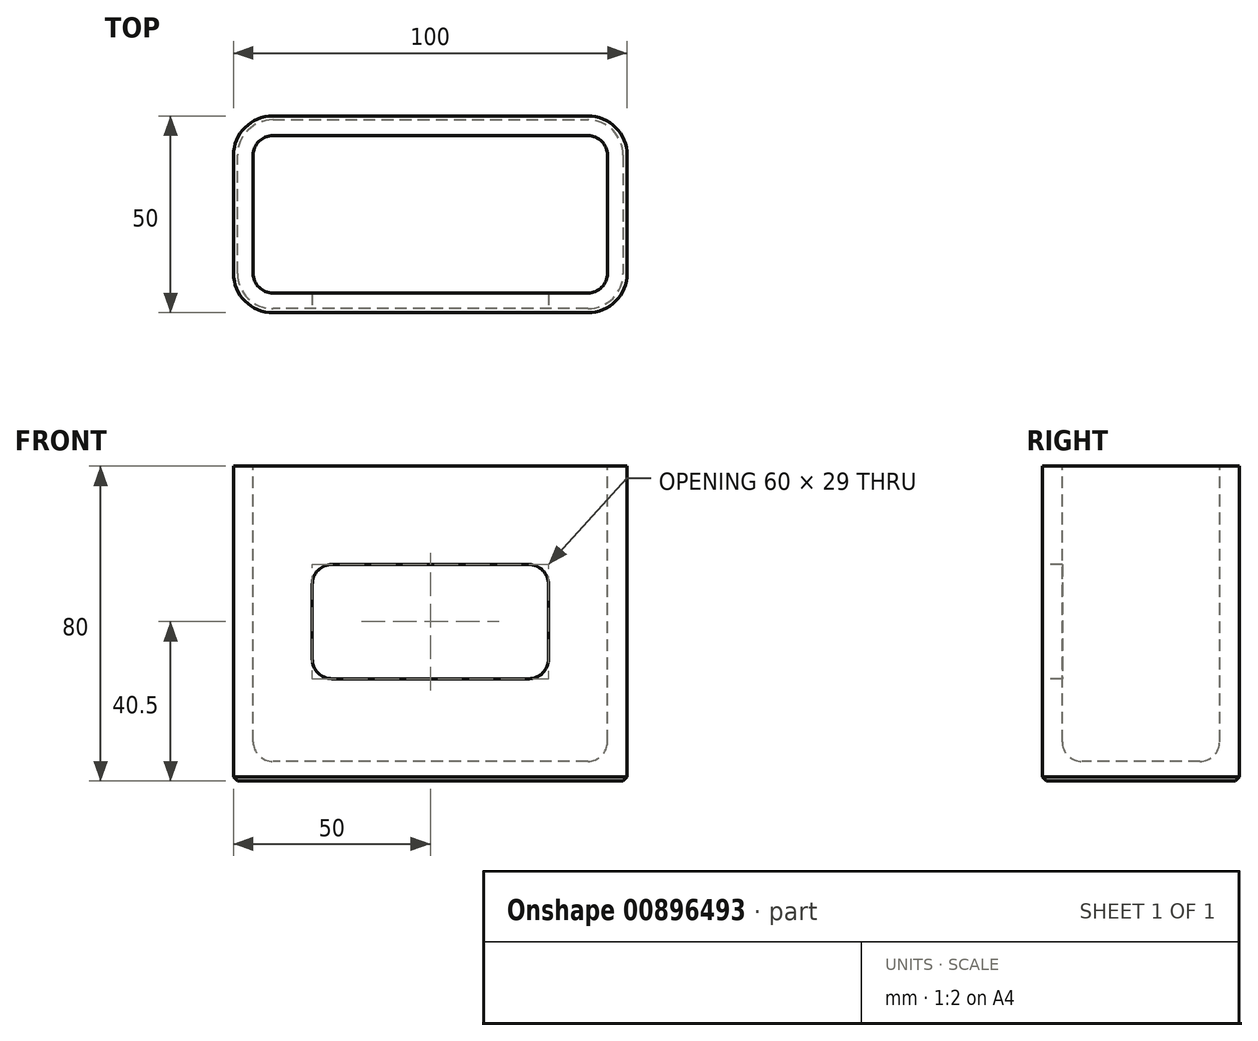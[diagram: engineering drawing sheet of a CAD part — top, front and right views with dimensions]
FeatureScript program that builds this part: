
annotation { "Feature Type Name" : "Feature", "Feature Type Description" : "" }
export const myFeature = defineFeature(function(context is Context, id is Id, definition is map)
    precondition{}
    {
        {
            var Q0;
            Q0=qCreatedBy(makeId("Top.planeOp"),FACE);
            var sketch = newSketch(context, id + "F0", { "sketchPlane" : qUnion([Q0])});
            skLineSegment(sketch, "E0.bottom", {"start": v(50, 25) * mm, "end": v(-50, 25) * mm});
            skLineSegment(sketch, "E0.top", {"start": v(50, -25) * mm, "end": v(-50, -25) * mm});
            skLineSegment(sketch, "E0.left", {"start": v(50, 25) * mm, "end": v(50, -25) * mm});
            skLineSegment(sketch, "E0.right", {"start": v(-50, 25) * mm, "end": v(-50, -25) * mm});
            skPoint(sketch, "E0.middle", {"position": v(0, 0) * mm});
            skSolve(sketch);
        }
        {
            var Q0;
            Q0 = qSketchRegion(id + "F0", true);
            extrude(context, id + "F1", {"entities" : qUnion([Q0]), "depth" : 80 * mm, "offsetDistance" : 25 * mm});
        }
        {
            var Q0;
            Q0=makeQuery(id+"F1.opExtrude","CAP_FACE",FACE,{"disambiguationData":[OSD([sQuery(id+"F0.wireOp",EDGE,"E0.bottom"),sQuery(id+"F0.wireOp",EDGE,"E0.top"),sQuery(id+"F0.wireOp",EDGE,"E0.left"),sQuery(id+"F0.wireOp",EDGE,"E0.right")])],"isStart":false});
            var sketch = newSketch(context, id + "F2", { "sketchPlane" : qUnion([Q0])});
            skLineSegment(sketch, "E1", {"start": v(-45, 20) * mm, "end": v(-45, -20) * mm});
            skLineSegment(sketch, "E2", {"start": v(-45, -20) * mm, "end": v(45, -20) * mm});
            skLineSegment(sketch, "E3", {"start": v(45, -20) * mm, "end": v(45, 20) * mm});
            skLineSegment(sketch, "E4", {"start": v(45, 20) * mm, "end": v(-45, 20) * mm});
            skSolve(sketch);
        }
        {
            var Q0;
            Q0 = qSketchRegion(id + "F2", true);
            extrude(context, id + "F3", {"entities" : qUnion([Q0]), "operationType" : NewBodyOperationType.REMOVE, "oppositeDirection" : true, "depth" : 75 * mm, "offsetDistance" : 25 * mm});
        }
        {
            var Q0;
            Q0=makeQuery(id+"F3.boolean.opBoolean","COPY",EDGE,{"derivedFrom":makeQuery(id+"F3.opExtrude","CAP_EDGE",EDGE,{"disambiguationData":[OSD([sQuery(id+"F2.wireOp",EDGE,"E3")])],"isStart":false})});
            var Q1;
            Q1=makeQuery(id+"F3.boolean.opBoolean","COPY",EDGE,{"derivedFrom":makeQuery(id+"F3.opExtrude","CAP_EDGE",EDGE,{"disambiguationData":[OSD([sQuery(id+"F2.wireOp",EDGE,"E4")])],"isStart":false})});
            var Q2;
            Q2=makeQuery(id+"F3.boolean.opBoolean","COPY",EDGE,{"derivedFrom":makeQuery(id+"F3.opExtrude","CAP_EDGE",EDGE,{"disambiguationData":[OSD([sQuery(id+"F2.wireOp",EDGE,"E2")])],"isStart":false})});
            var Q3;
            Q3=makeQuery(id+"F3.boolean.opBoolean","COPY",EDGE,{"derivedFrom":makeQuery(id+"F3.opExtrude","CAP_EDGE",EDGE,{"disambiguationData":[OSD([sQuery(id+"F2.wireOp",EDGE,"E1")])],"isStart":false})});
            var Q4;
            Q4=makeQuery(id+"F3.boolean.opBoolean","COPY",EDGE,{"derivedFrom":makeQuery(id+"F3.opExtrude","SWEPT_EDGE",EDGE,{"disambiguationData":[OSD([sQuery(id+"F2.wireOp",EDGE,"E1"),sQuery(id+"F2.wireOp",EDGE,"E4")])]})});
            var Q5;
            Q5=makeQuery(id+"F3.boolean.opBoolean","COPY",EDGE,{"derivedFrom":makeQuery(id+"F3.opExtrude","SWEPT_EDGE",EDGE,{"disambiguationData":[OSD([sQuery(id+"F2.wireOp",EDGE,"E1"),sQuery(id+"F2.wireOp",EDGE,"E2")])]})});
            var Q6;
            Q6=makeQuery(id+"F3.boolean.opBoolean","COPY",EDGE,{"derivedFrom":makeQuery(id+"F3.opExtrude","SWEPT_EDGE",EDGE,{"disambiguationData":[OSD([sQuery(id+"F2.wireOp",EDGE,"E3"),sQuery(id+"F2.wireOp",EDGE,"E4")])]})});
            var Q7;
            Q7=makeQuery(id+"F3.boolean.opBoolean","COPY",EDGE,{"derivedFrom":makeQuery(id+"F3.opExtrude","SWEPT_EDGE",EDGE,{"disambiguationData":[OSD([sQuery(id+"F2.wireOp",EDGE,"E2"),sQuery(id+"F2.wireOp",EDGE,"E3")])]})});
            var Q8;
            Q8=makeQuery(id+"F3.boolean.opBoolean","COPY",EDGE,{"derivedFrom":makeQuery(id+"F3.opExtrude","CAP_EDGE",EDGE,{"disambiguationData":[OSD([sQuery(id+"F2.wireOp",EDGE,"E3")])],"isStart":true})});
            var Q9;
            Q9=makeQuery(id+"F3.boolean.opBoolean","COPY",EDGE,{"derivedFrom":makeQuery(id+"F3.opExtrude","CAP_EDGE",EDGE,{"disambiguationData":[OSD([sQuery(id+"F2.wireOp",EDGE,"E4")])],"isStart":true})});
            var Q10;
            Q10=makeQuery(id+"F3.boolean.opBoolean","COPY",EDGE,{"derivedFrom":makeQuery(id+"F3.opExtrude","CAP_EDGE",EDGE,{"disambiguationData":[OSD([sQuery(id+"F2.wireOp",EDGE,"E1")])],"isStart":true})});
            var Q11;
            Q11=makeQuery(id+"F3.boolean.opBoolean","COPY",EDGE,{"derivedFrom":makeQuery(id+"F3.opExtrude","CAP_EDGE",EDGE,{"disambiguationData":[OSD([sQuery(id+"F2.wireOp",EDGE,"E2")])],"isStart":true})});
            fillet(context, id + "F4", {"entities" : qUnion([Q0, Q1, Q2, Q3, Q4, Q5, Q6, Q7, Q8, Q9, Q10, Q11]), "radius" : 5 * mm, "tangentPropagation" : true, "allowEdgeOverflow" : false});
        }
        {
            var Q0;
            Q0=makeQuery(id+"F1.opExtrude","SWEPT_EDGE",EDGE,{"disambiguationData":[OSD([sQuery(id+"F0.wireOp",EDGE,"E0.top"),sQuery(id+"F0.wireOp",EDGE,"E0.left")])]});
            var Q1;
            Q1=makeQuery(id+"F1.opExtrude","SWEPT_EDGE",EDGE,{"disambiguationData":[OSD([sQuery(id+"F0.wireOp",EDGE,"E0.top"),sQuery(id+"F0.wireOp",EDGE,"E0.right")])]});
            var Q2;
            Q2=makeQuery(id+"F1.opExtrude","SWEPT_EDGE",EDGE,{"disambiguationData":[OSD([sQuery(id+"F0.wireOp",EDGE,"E0.bottom"),sQuery(id+"F0.wireOp",EDGE,"E0.right")])]});
            var Q3;
            Q3=makeQuery(id+"F1.opExtrude","SWEPT_EDGE",EDGE,{"disambiguationData":[OSD([sQuery(id+"F0.wireOp",EDGE,"E0.bottom"),sQuery(id+"F0.wireOp",EDGE,"E0.left")])]});
            fillet(context, id + "F5", {"entities" : qUnion([Q0, Q1, Q2, Q3]), "radius" : 10 * mm, "tangentPropagation" : true, "allowEdgeOverflow" : false});
        }
        {
            var Q0;
            Q0=makeQuery(id+"F1.opExtrude","CAP_EDGE",EDGE,{"disambiguationData":[OSD([sQuery(id+"F0.wireOp",EDGE,"E0.top")])],"isStart":true});
            var Q1;
            {var subQ0=sQuery(id+"F0.wireOp",EDGE,"E0.left");var subQ1=sQuery(id+"F0.wireOp",EDGE,"E0.top");Q1=makeQuery(id+"F5.opFillet","BLEND_EDGE",EDGE,{"blendedFrom":[makeQuery(id+"F1.opExtrude","SWEPT_EDGE",EDGE,{"disambiguationData":[OSD([subQ1,subQ0])]}),makeQuery(id+"F1.opExtrude","CAP_FACE",FACE,{"disambiguationData":[OSD([sQuery(id+"F0.wireOp",EDGE,"E0.bottom"),subQ1,subQ0,sQuery(id+"F0.wireOp",EDGE,"E0.right")])],"isStart":true})],"blendedInto":[makeQuery(id+"F1.opExtrude","CAP_FACE",FACE,{"disambiguationData":[OSD([sQuery(id+"F0.wireOp",EDGE,"E0.bottom"),subQ1,subQ0,sQuery(id+"F0.wireOp",EDGE,"E0.right")])],"isStart":true})]});}
            var Q2;
            Q2=makeQuery(id+"F1.opExtrude","CAP_EDGE",EDGE,{"disambiguationData":[OSD([sQuery(id+"F0.wireOp",EDGE,"E0.left")])],"isStart":true});
            var Q3;
            {var subQ0=sQuery(id+"F0.wireOp",EDGE,"E0.left");var subQ1=sQuery(id+"F0.wireOp",EDGE,"E0.bottom");Q3=makeQuery(id+"F5.opFillet","BLEND_EDGE",EDGE,{"blendedFrom":[makeQuery(id+"F1.opExtrude","SWEPT_EDGE",EDGE,{"disambiguationData":[OSD([subQ1,subQ0])]}),makeQuery(id+"F1.opExtrude","CAP_FACE",FACE,{"disambiguationData":[OSD([subQ1,sQuery(id+"F0.wireOp",EDGE,"E0.top"),subQ0,sQuery(id+"F0.wireOp",EDGE,"E0.right")])],"isStart":true})],"blendedInto":[makeQuery(id+"F1.opExtrude","CAP_FACE",FACE,{"disambiguationData":[OSD([subQ1,sQuery(id+"F0.wireOp",EDGE,"E0.top"),subQ0,sQuery(id+"F0.wireOp",EDGE,"E0.right")])],"isStart":true})]});}
            var Q4;
            Q4=makeQuery(id+"F1.opExtrude","CAP_EDGE",EDGE,{"disambiguationData":[OSD([sQuery(id+"F0.wireOp",EDGE,"E0.bottom")])],"isStart":true});
            var Q5;
            {var subQ0=sQuery(id+"F0.wireOp",EDGE,"E0.right");var subQ1=sQuery(id+"F0.wireOp",EDGE,"E0.bottom");Q5=makeQuery(id+"F5.opFillet","BLEND_EDGE",EDGE,{"blendedFrom":[makeQuery(id+"F1.opExtrude","SWEPT_EDGE",EDGE,{"disambiguationData":[OSD([subQ1,subQ0])]}),makeQuery(id+"F1.opExtrude","CAP_FACE",FACE,{"disambiguationData":[OSD([subQ1,sQuery(id+"F0.wireOp",EDGE,"E0.top"),sQuery(id+"F0.wireOp",EDGE,"E0.left"),subQ0])],"isStart":true})],"blendedInto":[makeQuery(id+"F1.opExtrude","CAP_FACE",FACE,{"disambiguationData":[OSD([subQ1,sQuery(id+"F0.wireOp",EDGE,"E0.top"),sQuery(id+"F0.wireOp",EDGE,"E0.left"),subQ0])],"isStart":true})]});}
            var Q6;
            Q6=makeQuery(id+"F1.opExtrude","CAP_EDGE",EDGE,{"disambiguationData":[OSD([sQuery(id+"F0.wireOp",EDGE,"E0.right")])],"isStart":true});
            var Q7;
            {var subQ0=sQuery(id+"F0.wireOp",EDGE,"E0.right");var subQ1=sQuery(id+"F0.wireOp",EDGE,"E0.top");Q7=makeQuery(id+"F5.opFillet","BLEND_EDGE",EDGE,{"blendedFrom":[makeQuery(id+"F1.opExtrude","SWEPT_EDGE",EDGE,{"disambiguationData":[OSD([subQ1,subQ0])]}),makeQuery(id+"F1.opExtrude","CAP_FACE",FACE,{"disambiguationData":[OSD([sQuery(id+"F0.wireOp",EDGE,"E0.bottom"),subQ1,sQuery(id+"F0.wireOp",EDGE,"E0.left"),subQ0])],"isStart":true})],"blendedInto":[makeQuery(id+"F1.opExtrude","CAP_FACE",FACE,{"disambiguationData":[OSD([sQuery(id+"F0.wireOp",EDGE,"E0.bottom"),subQ1,sQuery(id+"F0.wireOp",EDGE,"E0.left"),subQ0])],"isStart":true})]});}
            chamfer(context, id + "F6", {"entities" : qUnion([Q0, Q1, Q2, Q3, Q4, Q5, Q6, Q7]), "width" : 1 * mm, "tangentPropagation" : true});
        }
        {
            var Q0;
            Q0=makeQuery(id+"F1.opExtrude","SWEPT_FACE",FACE,{"disambiguationData":[OSD([sQuery(id+"F0.wireOp",EDGE,"E0.top")])]});
            var sketch = newSketch(context, id + "F7", { "sketchPlane" : qUnion([Q0])});
            skLineSegment(sketch, "E5.bottom", {"start": v(-25, 55) * mm, "end": v(25, 55) * mm});
            skLineSegment(sketch, "E5.top", {"start": v(-25, 26) * mm, "end": v(25, 26) * mm});
            skLineSegment(sketch, "E5.left", {"start": v(-30, 50) * mm, "end": v(-30, 31) * mm});
            skLineSegment(sketch, "E5.right", {"start": v(30, 50) * mm, "end": v(30, 31) * mm});
            skPoint(sketch, "E6.visualSharp", {"position": v(-30, 55) * mm});
            skArc(sketch, "E6.filletArc", {"start": v(-25, 55) * mm, "mid": v(-28.54, 53.54) * mm, "end": v(-30, 50) * mm});
            skPoint(sketch, "E7.visualSharp", {"position": v(-30, 26) * mm});
            skArc(sketch, "E7.filletArc", {"start": v(-30, 31) * mm, "mid": v(-28.54, 27.46) * mm, "end": v(-25, 26) * mm});
            skPoint(sketch, "E8.visualSharp", {"position": v(30, 55) * mm});
            skArc(sketch, "E8.filletArc", {"start": v(30, 50) * mm, "mid": v(28.54, 53.54) * mm, "end": v(25, 55) * mm});
            skPoint(sketch, "E9.visualSharp", {"position": v(30, 26) * mm});
            skArc(sketch, "E9.filletArc", {"start": v(25, 26) * mm, "mid": v(28.54, 27.46) * mm, "end": v(30, 31) * mm});
            skSolve(sketch);
        }
        {
            var Q0;
            Q0 = qSketchRegion(id + "F7", true);
            extrude(context, id + "F8", {"entities" : qUnion([Q0]), "operationType" : NewBodyOperationType.REMOVE, "oppositeDirection" : true, "depth" : 5 * mm, "offsetDistance" : 25 * mm});
        }
    });
